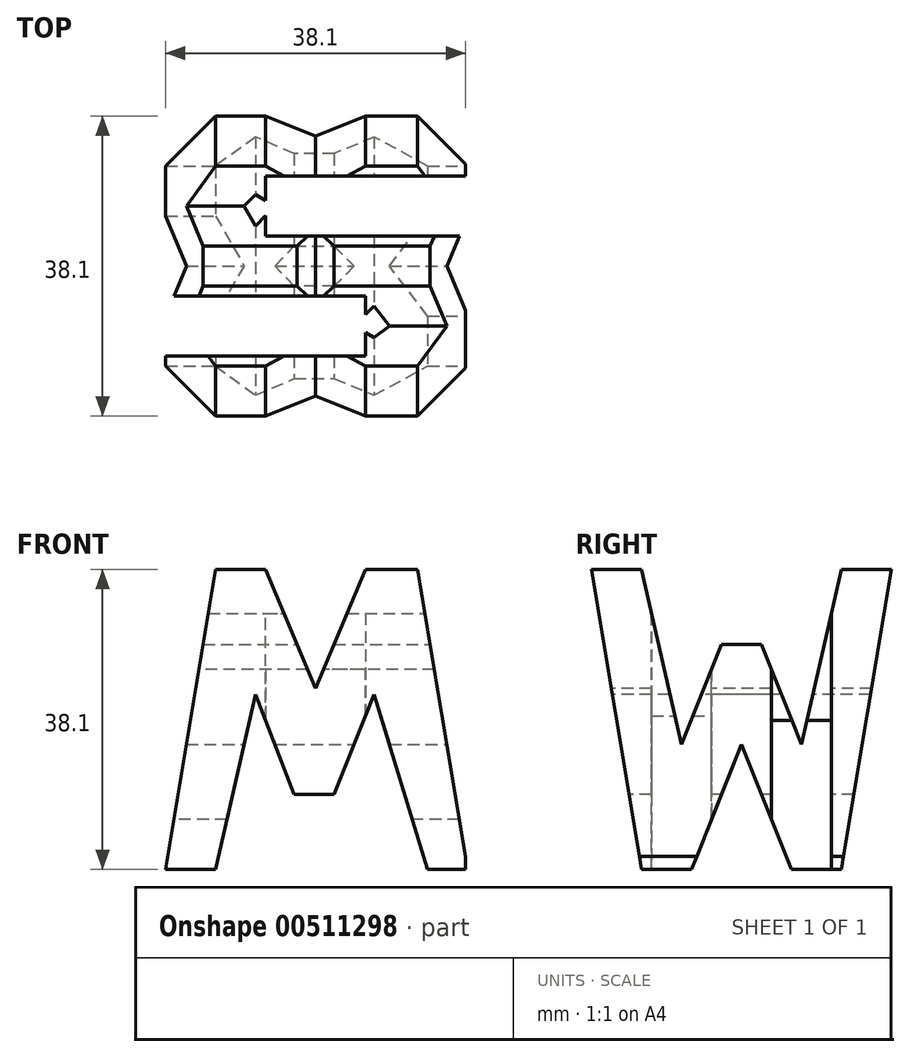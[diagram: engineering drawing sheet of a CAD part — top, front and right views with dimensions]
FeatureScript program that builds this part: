
annotation { "Feature Type Name" : "Feature", "Feature Type Description" : "" }
export const myFeature = defineFeature(function(context is Context, id is Id, definition is map)
    precondition{}
    {
        {
            var Q0;
            Q0=qCreatedBy(makeId("Front.planeOp"),FACE);
            var sketch = newSketch(context, id + "F0", { "sketchPlane" : qUnion([Q0])});
            skLineSegment(sketch, "E0", {"start": v(0, 0) * mm, "end": v(38.1, 0) * mm});
            skLineSegment(sketch, "E1", {"start": v(38.1, 0) * mm, "end": v(38.1, 38.1) * mm});
            skLineSegment(sketch, "E2", {"start": v(38.1, 38.1) * mm, "end": v(0, 38.1) * mm});
            skLineSegment(sketch, "E3", {"start": v(0, 38.1) * mm, "end": v(0, 0) * mm});
            skSolve(sketch);
        }
        {
            var Q0;
            Q0 = qSketchRegion(id + "F0", true);
            extrude(context, id + "F1", {"entities" : qUnion([Q0]), "depth" : 38.1 * mm, "offsetDistance" : 25.4 * mm});
        }
        {
            var Q0;
            Q0=qCreatedBy(makeId("Front.planeOp"),FACE);
            cPlane(context, id + "F2", {"entities" : qUnion([Q0]), "cplaneType" : CPlaneType.OFFSET, "offset" : 38.1 * mm, "width" : 152.4 * mm, "height" : 152.4 * mm});
        }
        {
            var Q0;
            Q0=qCreatedBy(makeId("Right.planeOp"),FACE);
            cPlane(context, id + "F3", {"entities" : qUnion([Q0]), "cplaneType" : CPlaneType.OFFSET, "offset" : 38.1 * mm, "width" : 152.4 * mm, "height" : 152.4 * mm});
        }
        {
            var Q0;
            Q0=qCreatedBy(makeId("Top.planeOp"),FACE);
            cPlane(context, id + "F4", {"entities" : qUnion([Q0]), "cplaneType" : CPlaneType.OFFSET, "offset" : 38.1 * mm, "width" : 152.4 * mm, "height" : 152.4 * mm});
        }
        {
            var Q0;
            Q0=qCreatedBy(id+"F3.planeOp",FACE);
            var sketch = newSketch(context, id + "F5", { "sketchPlane" : qUnion([Q0])});
            skLineSegment(sketch, "E4", {"start": v(0, 0) * mm, "end": v(0, 38.1) * mm});
            skLineSegment(sketch, "E5", {"start": v(0, 38.1) * mm, "end": v(-38.1, 38.1) * mm});
            skLineSegment(sketch, "E6", {"start": v(-38.1, 38.1) * mm, "end": v(-38.1, 0) * mm});
            skLineSegment(sketch, "E7", {"start": v(-38.1, 0) * mm, "end": v(0, 0) * mm});
            skLineSegment(sketch, "E8", {"start": v(-38.1, 38.1) * mm, "end": v(-31.75, 0) * mm});
            skLineSegment(sketch, "E9", {"start": v(-25.4, 0) * mm, "end": v(-19.05, 15.88) * mm});
            skLineSegment(sketch, "E10", {"start": v(-19.05, 15.88) * mm, "end": v(-12.7, 0) * mm});
            skLineSegment(sketch, "E11", {"start": v(-6.35, 0) * mm, "end": v(0, 38.1) * mm});
            skLineSegment(sketch, "E12", {"start": v(-31.75, 38.1) * mm, "end": v(-26.67, 15.88) * mm});
            skLineSegment(sketch, "E13", {"start": v(-26.67, 15.88) * mm, "end": v(-21.59, 28.58) * mm});
            skLineSegment(sketch, "E14", {"start": v(-21.59, 28.58) * mm, "end": v(-16.5, 28.58) * mm});
            skLineSegment(sketch, "E15", {"start": v(-16.5, 28.58) * mm, "end": v(-11.43, 15.88) * mm});
            skLineSegment(sketch, "E16", {"start": v(-11.43, 15.88) * mm, "end": v(-6.35, 38.1) * mm});
            skSolve(sketch);
        }
        {
            var Q0;
            {var subQ0=sQuery(id+"F5.wireOp",EDGE,"E12");Q0=makeQuery(id+"F5.imprint","IMPRINT",FACE,{"disambiguationData":[TD([[makeQuery(id+"F5.imprint","IMPRINT",EDGE,{"derivedFrom":subQ0}),1.0]])]});}
            var Q1;
            {var subQ0=sQuery(id+"F5.wireOp",EDGE,"E6");Q1=makeQuery(id+"F5.imprint","IMPRINT",FACE,{"disambiguationData":[TD([[makeQuery(id+"F5.imprint","IMPRINT",EDGE,{"derivedFrom":subQ0}),1.0]])]});}
            var Q2;
            {var subQ0=sQuery(id+"F5.wireOp",EDGE,"E9");Q2=makeQuery(id+"F5.imprint","IMPRINT",FACE,{"disambiguationData":[TD([[makeQuery(id+"F5.imprint","IMPRINT",EDGE,{"derivedFrom":subQ0}),-1.0]])]});}
            var Q3;
            {var subQ0=sQuery(id+"F5.wireOp",EDGE,"E4");Q3=makeQuery(id+"F5.imprint","IMPRINT",FACE,{"disambiguationData":[TD([[makeQuery(id+"F5.imprint","IMPRINT",EDGE,{"derivedFrom":subQ0}),1.0]])]});}
            extrude(context, id + "F6", {"entities" : qUnion([Q0, Q1, Q2, Q3]), "operationType" : NewBodyOperationType.REMOVE, "oppositeDirection" : true, "depth" : 38.1 * mm, "offsetDistance" : 25.4 * mm});
        }
        {
            var Q0;
            Q0=qCreatedBy(id+"F2.planeOp",FACE);
            var sketch = newSketch(context, id + "F7", { "sketchPlane" : qUnion([Q0])});
            skLineSegment(sketch, "E17", {"start": v(0, 0) * mm, "end": v(38.38, 0) * mm});
            skLineSegment(sketch, "E18", {"start": v(38.38, 0) * mm, "end": v(38.38, 38.1) * mm});
            skLineSegment(sketch, "E19", {"start": v(38.38, 38.1) * mm, "end": v(0, 38.1) * mm});
            skLineSegment(sketch, "E20", {"start": v(0, 38.1) * mm, "end": v(0, 0) * mm});
            skLineSegment(sketch, "E21", {"start": v(6.35, 38.1) * mm, "end": v(0, 0) * mm});
            skLineSegment(sketch, "E22", {"start": v(32.03, 38.1) * mm, "end": v(38.38, 0) * mm});
            skLineSegment(sketch, "E23", {"start": v(6.35, 0) * mm, "end": v(11.43, 22.22) * mm});
            skLineSegment(sketch, "E24", {"start": v(26.5, 22.22) * mm, "end": v(33.3, 0) * mm});
            skLineSegment(sketch, "E25", {"start": v(11.43, 22.22) * mm, "end": v(16.33, 9.52) * mm});
            skLineSegment(sketch, "E26", {"start": v(16.33, 9.52) * mm, "end": v(21.41, 9.52) * mm});
            skLineSegment(sketch, "E27", {"start": v(21.41, 9.52) * mm, "end": v(26.5, 22.22) * mm});
            skLineSegment(sketch, "E28", {"start": v(12.7, 38.1) * mm, "end": v(19.05, 23.02) * mm});
            skLineSegment(sketch, "E29", {"start": v(19.05, 23.02) * mm, "end": v(25.4, 38.1) * mm});
            skSolve(sketch);
        }
        {
            var Q0;
            {var subQ0=sQuery(id+"F7.wireOp",EDGE,"E28");Q0=makeQuery(id+"F7.imprint","IMPRINT",FACE,{"disambiguationData":[TD([[makeQuery(id+"F7.imprint","IMPRINT",EDGE,{"derivedFrom":subQ0}),1.0]])]});}
            var Q1;
            {var subQ0=sQuery(id+"F7.wireOp",EDGE,"E20");Q1=makeQuery(id+"F7.imprint","IMPRINT",FACE,{"disambiguationData":[TD([[makeQuery(id+"F7.imprint","IMPRINT",EDGE,{"derivedFrom":subQ0}),1.0]])]});}
            var Q2;
            {var subQ1=sQuery(id+"F7.wireOp",EDGE,"E23");Q2=makeQuery(id+"F7.imprint","IMPRINT",FACE,{"disambiguationData":[TD([[makeQuery(id+"F7.imprint","IMPRINT",EDGE,{"derivedFrom":subQ1}),-1.0]])]});}
            var Q3;
            {var subQ0=sQuery(id+"F7.wireOp",EDGE,"E18");Q3=makeQuery(id+"F7.imprint","IMPRINT",FACE,{"disambiguationData":[TD([[makeQuery(id+"F7.imprint","IMPRINT",EDGE,{"derivedFrom":subQ0}),1.0]])]});}
            extrude(context, id + "F8", {"entities" : qUnion([Q0, Q1, Q2, Q3]), "operationType" : NewBodyOperationType.REMOVE, "oppositeDirection" : true, "depth" : 38.1 * mm, "offsetDistance" : 25.4 * mm});
        }
        {
            var Q0;
            Q0=qCreatedBy(id+"F4.planeOp",FACE);
            var sketch = newSketch(context, id + "F9", { "sketchPlane" : qUnion([Q0])});
            skLineSegment(sketch, "E30", {"start": v(0, 0) * mm, "end": v(38.1, 0) * mm});
            skLineSegment(sketch, "E31", {"start": v(38.1, 0) * mm, "end": v(38.1, -38.1) * mm});
            skLineSegment(sketch, "E32", {"start": v(38.1, -38.1) * mm, "end": v(0, -38.1) * mm});
            skLineSegment(sketch, "E33", {"start": v(0, -38.1) * mm, "end": v(0, 0) * mm});
            skLineSegment(sketch, "E34", {"start": v(38.1, -7.62) * mm, "end": v(12.7, -7.62) * mm});
            skLineSegment(sketch, "E35", {"start": v(12.7, -7.62) * mm, "end": v(12.7, -15.24) * mm});
            skLineSegment(sketch, "E36", {"start": v(12.7, -15.24) * mm, "end": v(38.1, -15.24) * mm});
            skLineSegment(sketch, "E37", {"start": v(0, -22.86) * mm, "end": v(25.4, -22.86) * mm});
            skLineSegment(sketch, "E38", {"start": v(25.4, -22.86) * mm, "end": v(25.4, -30.48) * mm});
            skLineSegment(sketch, "E39", {"start": v(25.4, -30.48) * mm, "end": v(0, -30.48) * mm});
            skSolve(sketch);
        }
        {
            var Q0;
            {var subQ0=sQuery(id+"F9.wireOp",EDGE,"E34");Q0=makeQuery(id+"F9.imprint","IMPRINT",FACE,{"disambiguationData":[TD([[makeQuery(id+"F9.imprint","IMPRINT",EDGE,{"derivedFrom":subQ0}),1.0]])]});}
            var Q1;
            {var subQ0=sQuery(id+"F9.wireOp",EDGE,"E37");Q1=makeQuery(id+"F9.imprint","IMPRINT",FACE,{"disambiguationData":[TD([[makeQuery(id+"F9.imprint","IMPRINT",EDGE,{"derivedFrom":subQ0}),-1.0]])]});}
            extrude(context, id + "F10", {"entities" : qUnion([Q0, Q1]), "operationType" : NewBodyOperationType.REMOVE, "oppositeDirection" : true, "depth" : 38.1 * mm, "offsetDistance" : 25.4 * mm});
        }
    });
